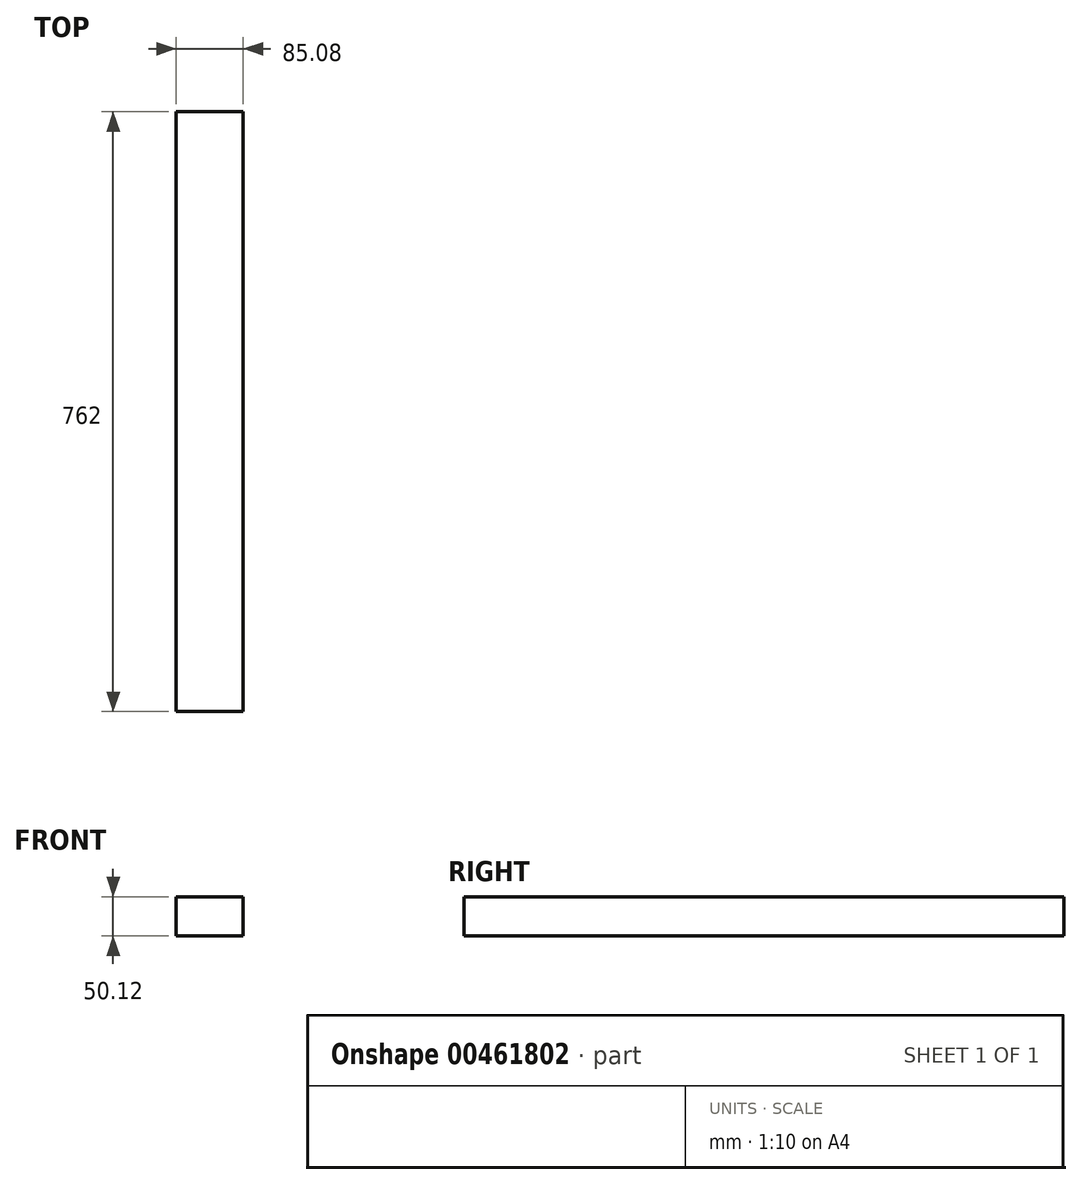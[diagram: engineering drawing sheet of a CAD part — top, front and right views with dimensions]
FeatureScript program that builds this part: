
annotation { "Feature Type Name" : "Feature", "Feature Type Description" : "" }
export const myFeature = defineFeature(function(context is Context, id is Id, definition is map)
    precondition{}
    {
        {
            var Q0;
            Q0=qCreatedBy(makeId("Front.planeOp"),FACE);
            var sketch = newSketch(context, id + "F0", { "sketchPlane" : qUnion([Q0])});
            skLineSegment(sketch, "E0.bottom", {"start": v(42.54, 25.06) * mm, "end": v(-42.54, 25.06) * mm});
            skLineSegment(sketch, "E0.top", {"start": v(42.54, -25.06) * mm, "end": v(-42.54, -25.06) * mm});
            skLineSegment(sketch, "E0.left", {"start": v(42.54, 25.06) * mm, "end": v(42.54, -25.06) * mm});
            skLineSegment(sketch, "E0.right", {"start": v(-42.54, 25.06) * mm, "end": v(-42.54, -25.06) * mm});
            skPoint(sketch, "E0.middle", {"position": v(0, 0) * mm});
            skSolve(sketch);
        }
        {
            var Q0;
            Q0 = qSketchRegion(id + "F0", true);
            extrude(context, id + "F1", {"entities" : qUnion([Q0]), "endBound" : BoundingType.SYMMETRIC, "depth" : 762 * mm});
        }
    });
